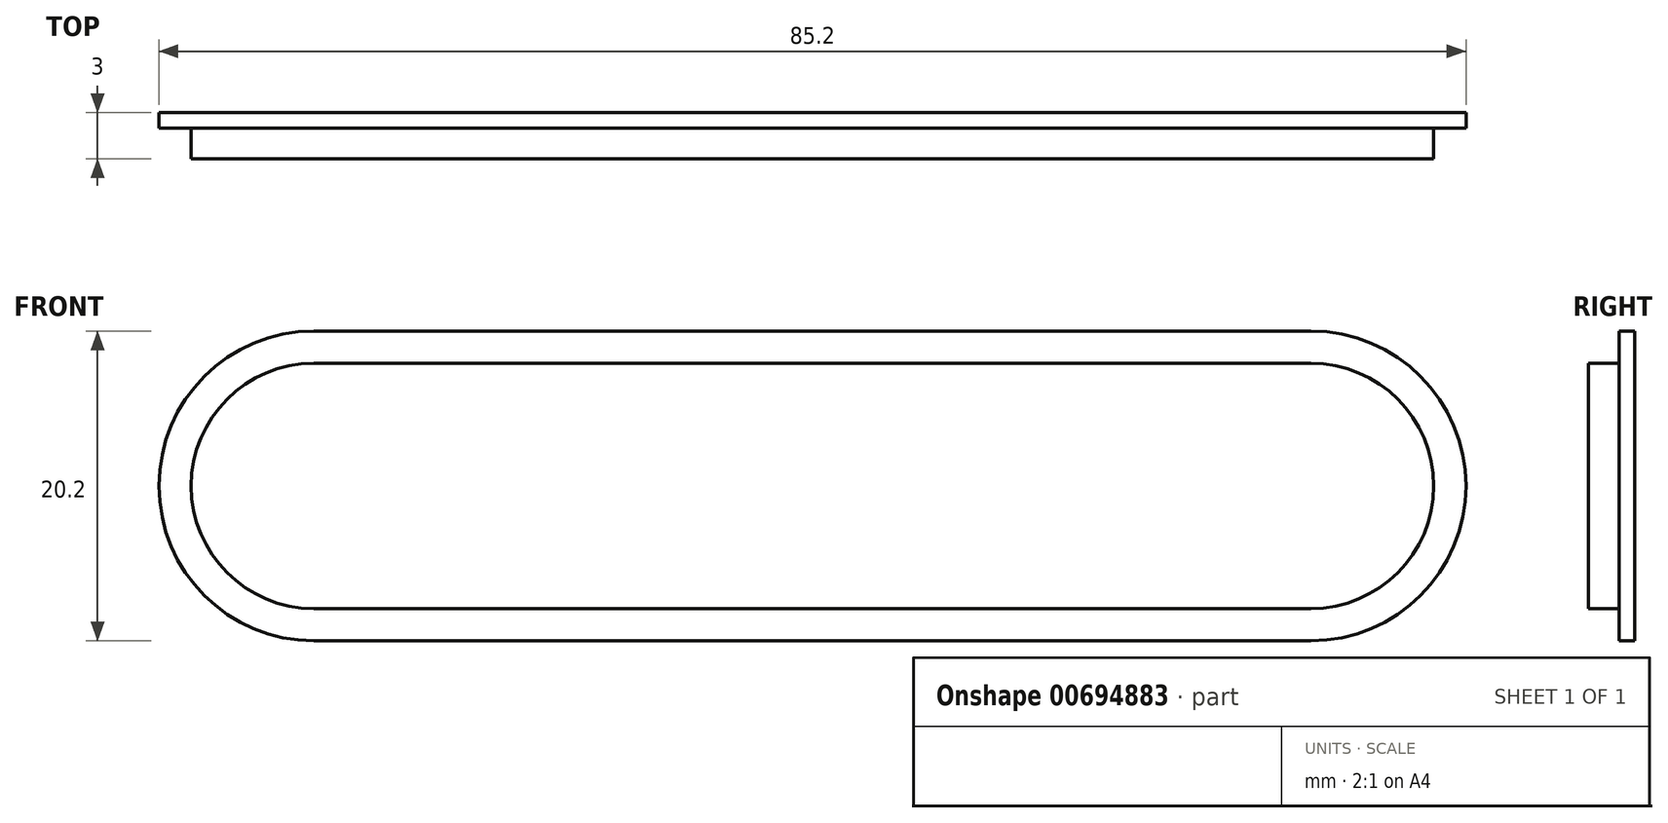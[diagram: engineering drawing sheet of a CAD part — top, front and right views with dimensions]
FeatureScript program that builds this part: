
annotation { "Feature Type Name" : "Feature", "Feature Type Description" : "" }
export const myFeature = defineFeature(function(context is Context, id is Id, definition is map)
    precondition{}
    {
        {
            var Q0;
            Q0=qCreatedBy(makeId("Front.planeOp"),FACE);
            var sketch = newSketch(context, id + "F0", { "sketchPlane" : qUnion([Q0])});
            skPoint(sketch, "E0.middle", {"position": v(0, 0) * mm});
            skLineSegment(sketch, "E1.bottom", {"start": v(-32.5, 12.5) * mm, "end": v(32.5, 12.5) * mm});
            skLineSegment(sketch, "E1.top", {"start": v(-32.5, -12.5) * mm, "end": v(32.5, -12.5) * mm});
            skLineSegment(sketch, "E2.bottom", {"start": v(-32.5, 10.5) * mm, "end": v(32.5, 10.5) * mm});
            skLineSegment(sketch, "E2.top", {"start": v(-32.5, -10.5) * mm, "end": v(32.5, -10.5) * mm});
            skArc(sketch, "E3", {"start": v(32.5, -12.5) * mm, "mid": v(45, 0) * mm, "end": v(32.5, 12.5) * mm});
            skArc(sketch, "E4", {"start": v(-32.5, 10.5) * mm, "mid": v(-43, 0) * mm, "end": v(-32.5, -10.5) * mm});
            skArc(sketch, "E5", {"start": v(-32.5, 12.5) * mm, "mid": v(-45, 0) * mm, "end": v(-32.5, -12.5) * mm});
            skArc(sketch, "E6", {"start": v(32.5, -10.5) * mm, "mid": v(43, 0) * mm, "end": v(32.5, 10.5) * mm});
            skLineSegment(sketch, "E7", {"start": v(-32.5, 10.5) * mm, "end": v(-32.5, 8.5) * mm});
            skLineSegment(sketch, "E8", {"start": v(-32.5, 8.5) * mm, "end": v(-32.5, 8) * mm});
            skLineSegment(sketch, "E9", {"start": v(-32.5, 8) * mm, "end": v(32.5, 8) * mm});
            skLineSegment(sketch, "E10", {"start": v(-32.5, 8.5) * mm, "end": v(32.5, 8.5) * mm});
            skLineSegment(sketch, "E11", {"start": v(32.5, -10.5) * mm, "end": v(32.5, -8.5) * mm});
            skLineSegment(sketch, "E12", {"start": v(32.5, -8.5) * mm, "end": v(32.5, -8) * mm});
            skLineSegment(sketch, "E13", {"start": v(32.5, -8) * mm, "end": v(-32.5, -8) * mm});
            skLineSegment(sketch, "E14", {"start": v(-32.5, -8.5) * mm, "end": v(32.5, -8.5) * mm});
            skArc(sketch, "E15", {"start": v(-32.5, 8) * mm, "mid": v(-40.5, 0) * mm, "end": v(-32.5, -8) * mm});
            skArc(sketch, "E16", {"start": v(-32.5, 8.5) * mm, "mid": v(-41, 0) * mm, "end": v(-32.5, -8.5) * mm});
            skArc(sketch, "E17", {"start": v(32.5, -8) * mm, "mid": v(40.5, 0) * mm, "end": v(32.5, 8) * mm});
            skArc(sketch, "E18", {"start": v(32.5, -8.5) * mm, "mid": v(41, 0) * mm, "end": v(32.5, 8.5) * mm});
            skLineSegment(sketch, "E19", {"start": v(-32.5, 10.5) * mm, "end": v(-32.5, 10.1) * mm});
            skLineSegment(sketch, "E20", {"start": v(32.5, 10.5) * mm, "end": v(32.5, 10.1) * mm});
            skLineSegment(sketch, "E21", {"start": v(32.5, 10.1) * mm, "end": v(-32.5, 10.1) * mm});
            skLineSegment(sketch, "E22", {"start": v(32.5, -10.5) * mm, "end": v(32.5, -10.1) * mm});
            skLineSegment(sketch, "E23", {"start": v(-32.5, -10.5) * mm, "end": v(-32.5, -10.1) * mm});
            skLineSegment(sketch, "E24", {"start": v(-32.5, -10.1) * mm, "end": v(32.5, -10.1) * mm});
            skArc(sketch, "E25", {"start": v(32.5, -10.1) * mm, "mid": v(42.6, 0) * mm, "end": v(32.5, 10.1) * mm});
            skArc(sketch, "E26", {"start": v(-32.5, 10.1) * mm, "mid": v(-42.6, 0) * mm, "end": v(-32.5, -10.1) * mm});
            skSolve(sketch);
        }
        {
            var Q0;
            {var subQ3=sQuery(id+"F0.wireOp",EDGE,"E14");Q0=makeQuery(id+"F0.imprint","IMPRINT",FACE,{"disambiguationData":[TD([[makeQuery(id+"F0.imprint","IMPRINT",EDGE,{"derivedFrom":subQ3}),-1.0]])]});}
            var Q1;
            {var subQ1=sQuery(id+"F0.wireOp",EDGE,"E10");Q1=makeQuery(id+"F0.imprint","IMPRINT",FACE,{"disambiguationData":[TD([[makeQuery(id+"F0.imprint","IMPRINT",EDGE,{"derivedFrom":subQ1}),1.0]])]});}
            var Q2;
            Q2=makeQuery(id+"F0.imprint","IMPRINT",FACE,{"disambiguationData":[TD([[makeQuery(id+"F0.imprint","IMPRINT",EDGE,{"derivedFrom":sQuery(id+"F0.wireOp",EDGE,"E8")}),1.0]])]});
            var Q3;
            Q3=makeQuery(id+"F0.imprint","IMPRINT",FACE,{"disambiguationData":[TD([[makeQuery(id+"F0.imprint","IMPRINT",EDGE,{"derivedFrom":sQuery(id+"F0.wireOp",EDGE,"E8")}),-1.0]])]});
            extrude(context, id + "F1", {"entities" : qUnion([Q0, Q1, Q2, Q3]), "depth" : 1 * mm, "offsetDistance" : 25 * mm});
        }
        {
            var Q0;
            Q0=makeQuery(id+"F0.imprint","IMPRINT",FACE,{"disambiguationData":[TD([[makeQuery(id+"F0.imprint","IMPRINT",EDGE,{"derivedFrom":sQuery(id+"F0.wireOp",EDGE,"E9")}),-1.0]])]});
            extrude(context, id + "F2", {"entities" : qUnion([Q0]), "operationType" : NewBodyOperationType.ADD, "depth" : 3 * mm, "offsetDistance" : 25 * mm});
        }
    });
